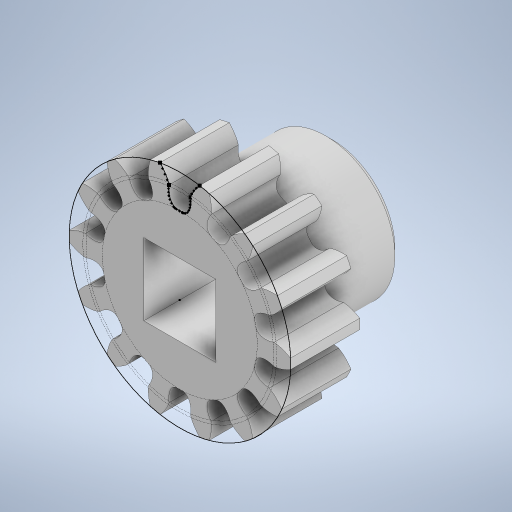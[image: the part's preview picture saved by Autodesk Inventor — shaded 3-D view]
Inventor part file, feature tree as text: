
AUTODESK INVENTOR PART (.ipt)
format: ipt  version: 2023 (Build 270158000, 158)  size: 1,170,432 bytes
history: native  units: in
note: dims shown in document units (in); Inventor stores cm internally (conversion verified against a paired STEP export)
features: sketch x5, extrude x5, pattern_circular x1, chamfer x1
ambient origin geometry x8: Origin, YZ Plane, XZ Plane, XY Plane, X Axis, Y Axis, Z Axis, Center Point
bodies: Solid1 (feature_tree)
feature tree (12):
  sketch  "Sketch1"  dims[d0=0.25in d1=0.0in]
  extrude  "Extrusion1"  TaperAngle=0.0deg  [1 undecoded]
  extrude  "Extrusion2"  Depth=5.5118in TaperAngle=360.0deg
  pattern_circular  "Circular Pattern1"  [2 undecoded]
  sketch  "Sketch2"  dims[d2=0.0in d3=0.0in d4=5.5118in d5=360.0deg]
  extrude  "Extrusion3"  Depth=0.1in TaperAngle=0.0deg
  extrude  "Extrusion5"  Depth=0.1in TaperAngle=45.0deg
  chamfer  "Chamfer2"  Distance=0.13in
  extrude  "Extrusion6"  Depth=0.13in
  sketch  "Sketch3"  dims[d7=0.26in]
  sketch  "Sketch5"  dims[d8=0.26in]
  sketch  "Sketch6"  dims[d9=0.15in d10=0.0in d15=0.5in d16=0.3in d17=0.0in d21=0.0236in d22=0.125in d23=45.0deg d24=0.13in d25=0.13in d26=0.1in d27=0.0in]
note: 3 required parameter values undecoded (feature->parameter linkage not recoverable at this tier; creation-order binding heuristic only, values carry confidence <= 0.55)
